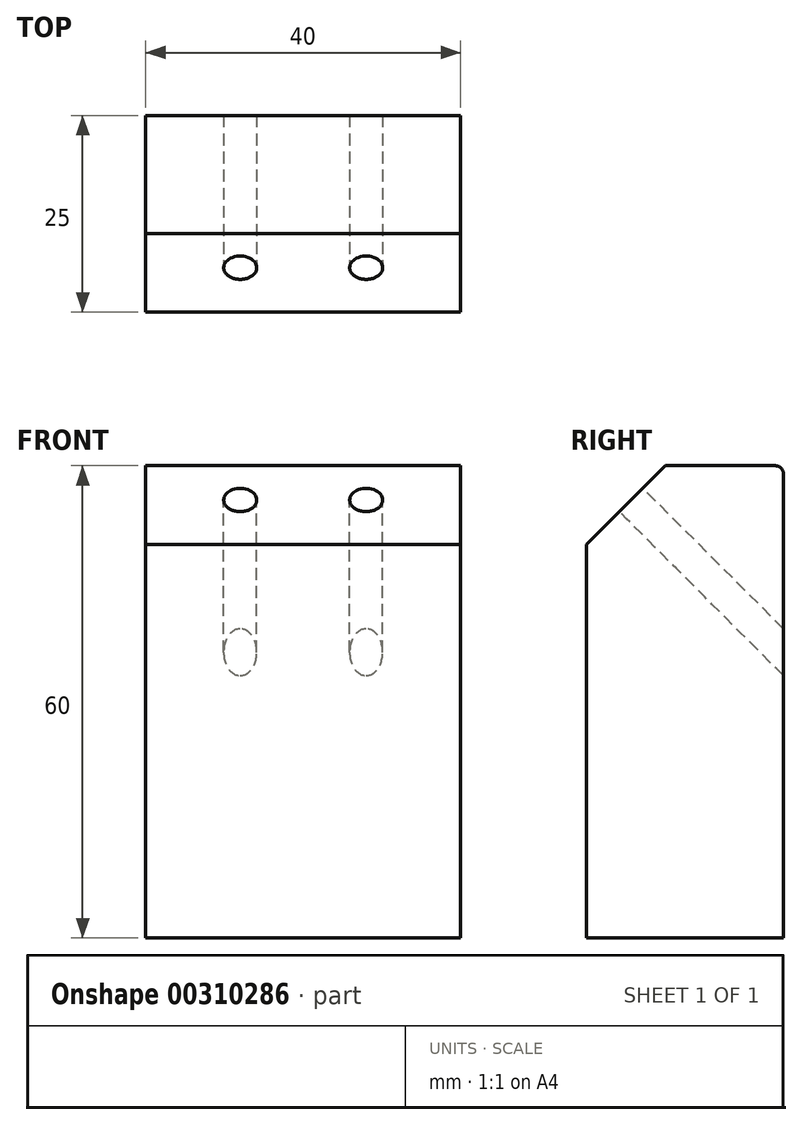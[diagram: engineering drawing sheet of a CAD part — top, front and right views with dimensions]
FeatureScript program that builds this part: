
annotation { "Feature Type Name" : "Feature", "Feature Type Description" : "" }
export const myFeature = defineFeature(function(context is Context, id is Id, definition is map)
    precondition{}
    {
        {
            var Q0;
            Q0=qCreatedBy(makeId("Front.planeOp"),FACE);
            var sketch = newSketch(context, id + "F0", { "sketchPlane" : qUnion([Q0])});
            skLineSegment(sketch, "E0", {"start": v(0, 0) * mm, "end": v(0, 60) * mm});
            skLineSegment(sketch, "E1", {"start": v(0, 60) * mm, "end": v(-40, 60) * mm});
            skLineSegment(sketch, "E2", {"start": v(-40, 60) * mm, "end": v(-40, 0) * mm});
            skLineSegment(sketch, "E3", {"start": v(-40, 0) * mm, "end": v(0, 0) * mm});
            skSolve(sketch);
        }
        {
            var Q0;
            Q0=makeQuery(id+"F0.imprint","IMPRINT",FACE,{"disambiguationData":[TD([[makeQuery(id+"F0.imprint","IMPRINT",EDGE,{"derivedFrom":sQuery(id+"F0.wireOp",EDGE,"E0")}),1.0]])]});
            extrude(context, id + "F1", {"entities" : qUnion([Q0]), "depth" : 25 * mm});
        }
        {
            var Q0;
            Q0=makeQuery(id+"F1.opExtrude","CAP_EDGE",EDGE,{"disambiguationData":[OSD([sQuery(id+"F0.wireOp",EDGE,"E1")])],"isStart":false});
            chamfer(context, id + "F2", {"entities" : qUnion([Q0]), "width" : 10 * mm, "tangentPropagation" : true});
        }
        {
            var Q0;
            Q0=makeQuery(id+"F2.opChamfer","BLEND_FACE",FACE,{"disambiguationData":[OSD([sQuery(id+"F0.wireOp",EDGE,"E1")])]});
            var sketch = newSketch(context, id + "F3", { "sketchPlane" : qUnion([Q0])});
            skPoint(sketch, "E4", {"position": v(-28, 25.68) * mm});
            skPoint(sketch, "E5", {"position": v(-12, 25.68) * mm});
            skSolve(sketch);
        }
        {
            var Q0;
            Q0=sQuery(id+"F3.wireOp",VERTEX,"E5");
            var Q1;
            Q1=sQuery(id+"F3.wireOp",VERTEX,"E4");
            var Q2;
            Q2=makeQuery(id+"F1.opExtrude","SWEPT_BODY",BODY,{"disambiguationData":[OSD([sQuery(id+"F0.wireOp",EDGE,"E0"),sQuery(id+"F0.wireOp",EDGE,"E1"),sQuery(id+"F0.wireOp",EDGE,"E2"),sQuery(id+"F0.wireOp",EDGE,"E3")])]});
            hole(context, id + "F4", {"style" : HoleStyle.SIMPLE, "endStyle" : HoleEndStyle.THROUGH, "standardTappedOrClearance" : lookupTablePath({ "standard" : "ISO", "engagement" : "75%", "pitch" : "0.8 mm", "size" : "M5", "type" : "Tapped" }), "standardBlindInLast" : lookupTablePath({ "standard" : "ISO", "engagement" : "75%", "pitch" : "0.8 mm", "size" : "M5", "type" : "Tapped" }), "holeDiameter" : 4.2 * mm, "showTappedDepth" : true, "tappedDepth" : 12 * mm, "tapClearance" : 3, "locations" : qUnion([Q0, Q1]), "scope" : qUnion([Q2]), "majorDiameter" : 5 * mm});
        }
        {
            var Q0;
            Q0=makeQuery(id+"F1.opExtrude","CAP_EDGE",EDGE,{"disambiguationData":[OSD([sQuery(id+"F0.wireOp",EDGE,"E1")])],"isStart":true});
            fillet(context, id + "F5", {"entities" : qUnion([Q0]), "radius" : 1 * mm, "tangentPropagation" : true, "allowEdgeOverflow" : false});
        }
    });
